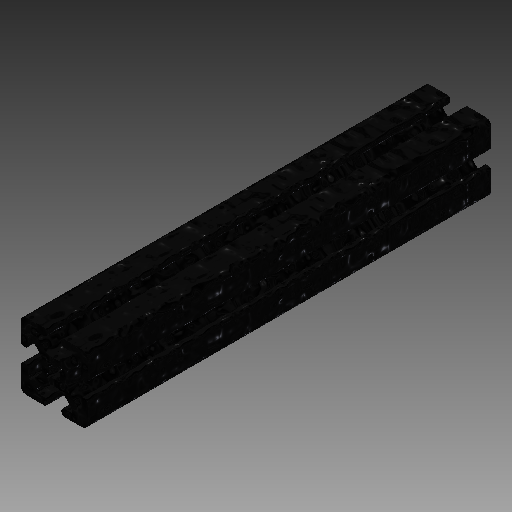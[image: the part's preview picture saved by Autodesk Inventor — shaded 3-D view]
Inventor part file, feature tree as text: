
AUTODESK INVENTOR PART (.ipt)
format: ipt  version: 2019 (Build 230136000, 136)  size: 281,600 bytes
history: native  units: in
note: dims shown in document units (in); Inventor stores cm internally (conversion verified against a paired STEP export)
features: plane x1, extrude x1, sketch x1
ambient origin geometry x8: Origin, YZ Plane, XZ Plane, XY Plane, X Axis, Y Axis, Z Axis, Center Point
bodies: Solid1 (feature_tree)
feature tree (3):
  plane  "Work Plane1"
  extrude  "Extrusion1"  [1 undecoded]
  sketch  "Sketch1"  dims[d0=9.0in d1=0.0in]
note: 1 required parameter value undecoded (feature->parameter linkage not recoverable at this tier; creation-order binding heuristic only, values carry confidence <= 0.55)
